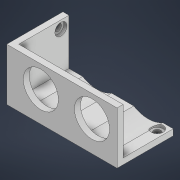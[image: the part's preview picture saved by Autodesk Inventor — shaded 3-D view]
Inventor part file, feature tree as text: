
AUTODESK INVENTOR PART (.ipt)
format: ipt  version: 2022 (Build 260153000, 153)  size: 163,328 bytes
history: native  units: mm
features: sketch x5, extrude x3, hole x2, projected_geometry x1
ambient origin geometry x8: Origin, YZ Plane, XZ Plane, XY Plane, X Axis, Y Axis, Z Axis, Center Point
bodies: Volumenkörper1 (feature_tree)
feature tree (11):
  extrude  "Extrusion1"  Depth=17.0mm
  extrude  "Extrusion2"  Depth=3.0mm TaperAngle=0.0deg
  hole  "Bohrung1"  [1 undecoded]
  hole  "Bohrung2"  [1 undecoded]
  extrude  "Extrusion3"  Depth=4.0mm
  sketch  "Skizze1"  dims[d1=17.5mm d5=17.0mm]
  sketch  "Skizze2"  dims[d7=11.0mm d8=3.0mm d9=0.0mm]
  projected_geometry  "Projizierte Kontur1"
  sketch  "Skizze3"  dims[d11=3.0mm d12=25.0mm d13=0.0mm]
  sketch  "Skizze4"  dims[d14=12.5mm]
  sketch  "Skizze5"  dims[d15=3.5mm d16=6.0mm d17=6.0mm d18=1.5mm d19=90.0deg d20=8.0mm d21=20.594885mm d22=4.0mm d23=4.0mm d24=3.5mm d25=6.0mm d26=6.0mm d27=1.5mm d28=90.0deg d29=8.0mm d30=20.594885mm d31=4.0mm d32=4.0mm d33=28.0mm d34=28.0mm d35=25.0mm d36=0.0mm]
note: 2 required parameter values undecoded (feature->parameter linkage not recoverable at this tier; creation-order binding heuristic only, values carry confidence <= 0.55)
